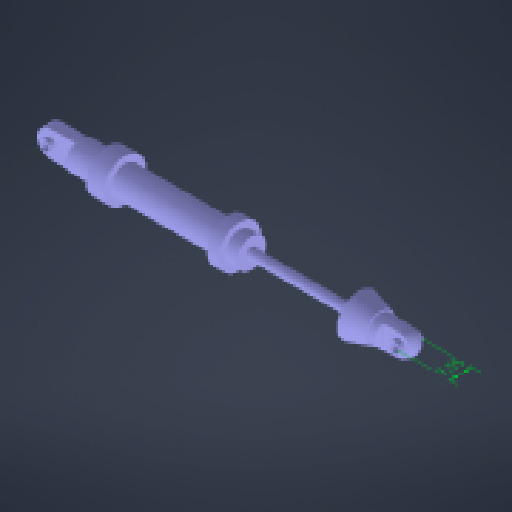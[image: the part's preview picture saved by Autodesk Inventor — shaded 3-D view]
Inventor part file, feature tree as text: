
AUTODESK INVENTOR PART (.ipt)
format: ipt  version: 2024 (Build 280153000, 153)  size: 354,816 bytes
history: native  units: mm
features: sketch x8, extrude x7, other x3, fillet x2, revolve x1, projected_geometry x1
ambient origin geometry x8: Origin, YZ Plane, XZ Plane, XY Plane, X Axis, Y Axis, Z Axis, Center Point
bodies: Body1 (feature_tree)
feature tree (22):
  other  "Твердое тело1"
  other  "Аннотации"
  revolve  "Вращение1"
  extrude  "Выдавливание1"  Depth=10.0mm
  extrude  "Выдавливание2"  TaperAngle=90.0deg  [1 undecoded]
  extrude  "Выдавливание3"  Depth=6.0mm
  extrude  "Выдавливание5"  Depth=102.0mm
  extrude  "Выдавливание6"  Depth=36.5mm
  fillet  "Сопряжение1"  Radius=15.0mm
  fillet  "Сопряжение2"  Radius=54.0mm
  extrude  "Выдавливание7"  Depth=4.0mm
  extrude  "Выдавливание8"  Depth=14.5mm
  sketch  "Эскиз1"
  sketch  "Эскиз2"
  sketch  "Эскиз3"
  projected_geometry  "Спроецированная петля1"
  sketch  "Эскиз4"
  sketch  "Эскиз7"
  sketch  "Эскиз8"
  sketch  "Эскиз9"
  sketch  "Эскиз10"
  other  "Линейный размер 1"
note: 1 required parameter value undecoded (feature->parameter linkage not recoverable at this tier; creation-order binding heuristic only, values carry confidence <= 0.55)
